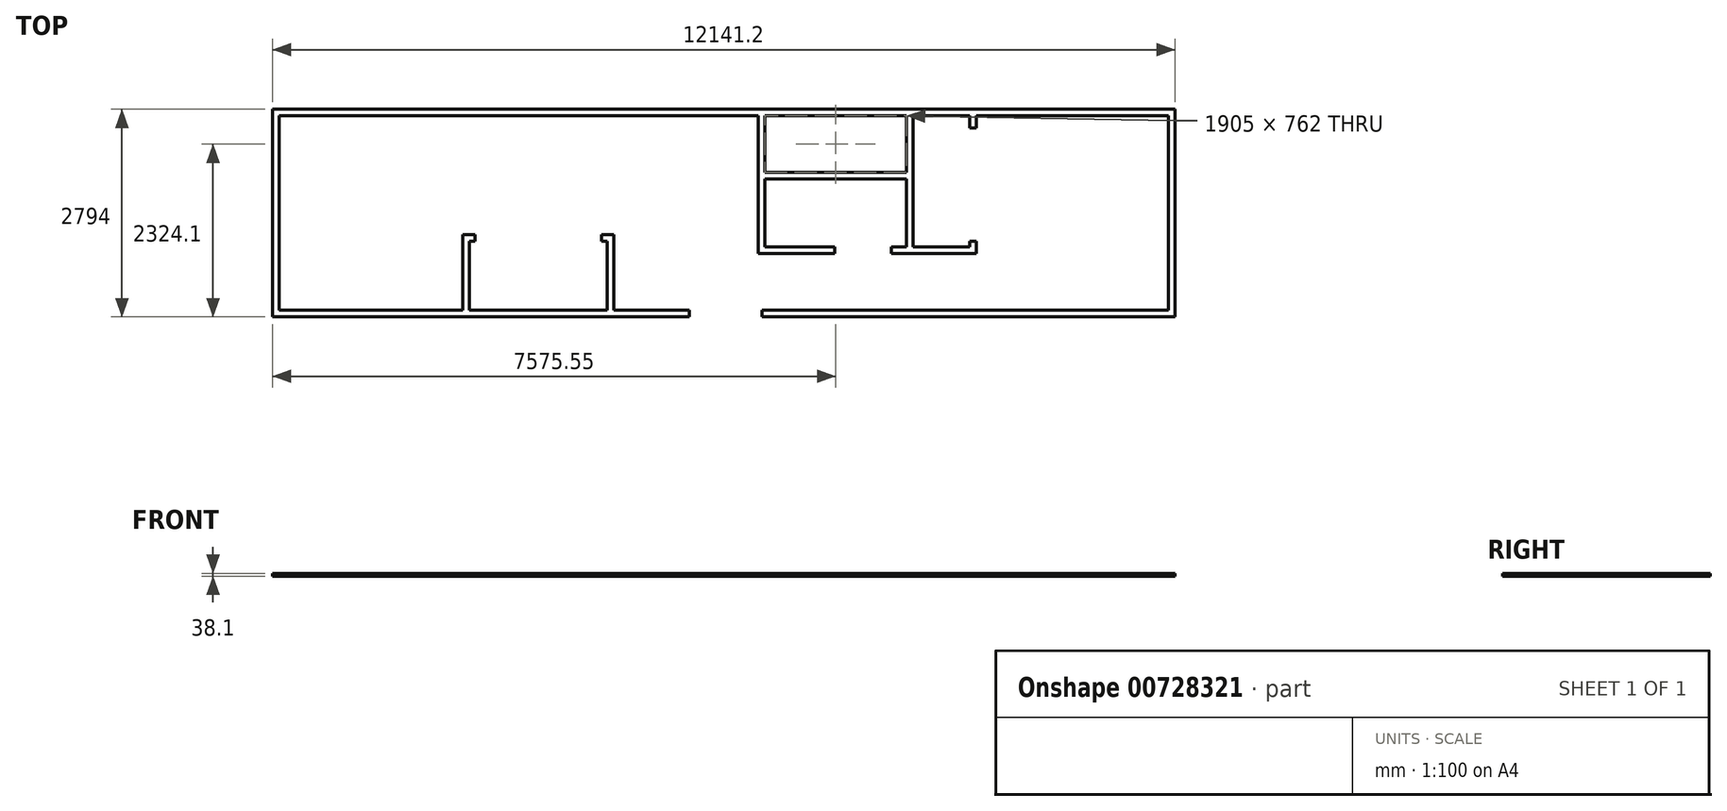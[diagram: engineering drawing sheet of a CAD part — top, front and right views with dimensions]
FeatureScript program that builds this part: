
annotation { "Feature Type Name" : "Feature", "Feature Type Description" : "" }
export const myFeature = defineFeature(function(context is Context, id is Id, definition is map)
    precondition{}
    {
        {
            var Q0;
            Q0=qCreatedBy(makeId("Top.planeOp"),FACE);
            var sketch = newSketch(context, id + "F0", { "sketchPlane" : qUnion([Q0])});
            skLineSegment(sketch, "E0.bottom", {"start": v(-6070.6, -1397) * mm, "end": v(-463.55, -1397) * mm});
            skLineSegment(sketch, "E0.top", {"start": v(-6070.6, 1397) * mm, "end": v(6070.6, 1397) * mm});
            skLineSegment(sketch, "E0.left", {"start": v(-6070.6, -1397) * mm, "end": v(-6070.6, 1397) * mm});
            skLineSegment(sketch, "E0.right", {"start": v(6070.6, -1397) * mm, "end": v(6070.6, 1397) * mm});
            skPoint(sketch, "E0.middle", {"position": v(0, 0) * mm});
            skLineSegment(sketch, "E1.0", {"start": v(-5981.7, -1308.1) * mm, "end": v(-5981.7, 1308.1) * mm});
            skLineSegment(sketch, "E1.1", {"start": v(-5981.7, -1308.1) * mm, "end": v(-463.55, -1308.1) * mm});
            skLineSegment(sketch, "E1.2", {"start": v(5981.7, -1308.1) * mm, "end": v(5981.7, 1308.1) * mm});
            skLineSegment(sketch, "E1.3", {"start": v(-5981.7, 1308.1) * mm, "end": v(463.55, 1308.1) * mm});
            skLineSegment(sketch, "E2.top", {"start": v(3397.25, -546.1) * mm, "end": v(3308.35, -546.1) * mm});
            skLineSegment(sketch, "E2.left", {"start": v(3397.25, 1308.1) * mm, "end": v(3397.25, 1143) * mm});
            skLineSegment(sketch, "E2.right", {"start": v(3308.35, 1308.1) * mm, "end": v(3308.35, 1143) * mm});
            skLineSegment(sketch, "E3.top", {"start": v(2457.45, -546.1) * mm, "end": v(2546.35, -546.1) * mm});
            skLineSegment(sketch, "E3.left", {"start": v(2457.45, 1308.1) * mm, "end": v(2457.45, 546.1) * mm});
            skLineSegment(sketch, "E3.right", {"start": v(2546.35, 1308.1) * mm, "end": v(2546.35, -457.2) * mm});
            skLineSegment(sketch, "E4", {"start": v(2546.35, -546.1) * mm, "end": v(3308.35, -546.1) * mm});
            skLineSegment(sketch, "E5.0", {"start": v(2546.35, -457.2) * mm, "end": v(3308.35, -457.2) * mm});
            skLineSegment(sketch, "E6.trimOffspring", {"start": v(2546.35, 1308.1) * mm, "end": v(3308.35, 1308.1) * mm});
            skLineSegment(sketch, "E7.trimOffspring", {"start": v(3397.25, 1308.1) * mm, "end": v(5981.7, 1308.1) * mm});
            skLineSegment(sketch, "E8", {"start": v(3308.35, 1143) * mm, "end": v(3397.25, 1143) * mm});
            skLineSegment(sketch, "E9", {"start": v(3308.35, -381) * mm, "end": v(3397.25, -381) * mm});
            skLineSegment(sketch, "E10", {"start": v(2457.45, -546.1) * mm, "end": v(2254.25, -546.1) * mm});
            skLineSegment(sketch, "E11", {"start": v(2457.45, -457.2) * mm, "end": v(2254.25, -457.2) * mm});
            skLineSegment(sketch, "E12", {"start": v(2254.25, -457.2) * mm, "end": v(2254.25, -546.1) * mm});
            skLineSegment(sketch, "E13.bottom", {"start": v(552.45, 546.1) * mm, "end": v(2457.45, 546.1) * mm});
            skLineSegment(sketch, "E14.trimOffspring", {"start": v(3308.35, -381) * mm, "end": v(3308.35, -457.2) * mm});
            skLineSegment(sketch, "E15.trimOffspring", {"start": v(3397.25, -381) * mm, "end": v(3397.25, -546.1) * mm});
            skLineSegment(sketch, "E16.trimOffspring", {"start": v(514.35, -1308.1) * mm, "end": v(5981.7, -1308.1) * mm});
            skLineSegment(sketch, "E17", {"start": v(-463.55, -1308.1) * mm, "end": v(-463.55, -1397) * mm});
            skLineSegment(sketch, "E18.trimOffspring", {"start": v(2457.45, 461.18) * mm, "end": v(2457.45, -457.2) * mm});
            skLineSegment(sketch, "E19.trimOffspring", {"start": v(552.45, 1308.1) * mm, "end": v(2457.45, 1308.1) * mm});
            skLineSegment(sketch, "E20", {"start": v(514.35, -1308.1) * mm, "end": v(514.35, -1397) * mm});
            skLineSegment(sketch, "E21.bottom", {"start": v(-1479.55, -1308.1) * mm, "end": v(-1568.45, -1308.1) * mm});
            skLineSegment(sketch, "E21.top", {"start": v(-1479.55, -292.1) * mm, "end": v(-1568.45, -292.1) * mm});
            skLineSegment(sketch, "E21.left", {"start": v(-1479.55, -1308.1) * mm, "end": v(-1479.55, -292.1) * mm});
            skLineSegment(sketch, "E21.right", {"start": v(-1568.45, -1308.1) * mm, "end": v(-1568.45, -292.1) * mm});
            skLineSegment(sketch, "E22.bottom", {"start": v(-3511.55, -292.1) * mm, "end": v(-3422.65, -292.1) * mm});
            skLineSegment(sketch, "E22.top", {"start": v(-3511.55, -1308.1) * mm, "end": v(-3422.65, -1308.1) * mm});
            skLineSegment(sketch, "E22.left", {"start": v(-3511.55, -292.1) * mm, "end": v(-3511.55, -1308.1) * mm});
            skLineSegment(sketch, "E22.right", {"start": v(-3422.65, -292.1) * mm, "end": v(-3422.65, -1308.1) * mm});
            skLineSegment(sketch, "E23", {"start": v(-3422.65, -292.1) * mm, "end": v(-3346.45, -292.1) * mm});
            skLineSegment(sketch, "E24", {"start": v(-3346.45, -292.1) * mm, "end": v(-3346.45, -381) * mm});
            skLineSegment(sketch, "E25", {"start": v(-3346.45, -381) * mm, "end": v(-3422.65, -381) * mm});
            skLineSegment(sketch, "E26.bottom", {"start": v(-1568.45, -292.1) * mm, "end": v(-1644.65, -292.1) * mm});
            skLineSegment(sketch, "E26.top", {"start": v(-1568.45, -381) * mm, "end": v(-1644.65, -381) * mm});
            skLineSegment(sketch, "E26.left", {"start": v(-1568.45, -292.1) * mm, "end": v(-1568.45, -381) * mm});
            skLineSegment(sketch, "E26.right", {"start": v(-1644.65, -292.1) * mm, "end": v(-1644.65, -381) * mm});
            skLineSegment(sketch, "E27", {"start": v(-3422.65, 1308.1) * mm, "end": v(-3422.65, 1397) * mm});
            skLineSegment(sketch, "E28", {"start": v(-4997.45, 1308.1) * mm, "end": v(-4997.45, 1397) * mm});
            skLineSegment(sketch, "E29.trimOffspring", {"start": v(514.35, -1397) * mm, "end": v(6070.6, -1397) * mm});
            skLineSegment(sketch, "E30", {"start": v(1492.25, -545.75) * mm, "end": v(1492.25, -456.85) * mm});
            skLineSegment(sketch, "E31", {"start": v(463.55, 1308.1) * mm, "end": v(463.55, -545.75) * mm});
            skLineSegment(sketch, "E32", {"start": v(463.55, -545.75) * mm, "end": v(1492.25, -545.75) * mm});
            skLineSegment(sketch, "E33", {"start": v(1492.25, -456.85) * mm, "end": v(552.45, -456.85) * mm});
            skLineSegment(sketch, "E34", {"start": v(552.45, -456.85) * mm, "end": v(552.45, 1308.1) * mm});
            skLineSegment(sketch, "E35", {"start": v(2457.45, 461.18) * mm, "end": v(552.45, 461.18) * mm});
            skSolve(sketch);
        }
        {
            var Q0;
            Q0=qSketchRegion(id+"F0",true);
            extrude(context, id + "F1", {"entities" : qUnion([Q0]), "depth" : 38.1 * mm, "offsetDistance" : 25.4 * mm});
        }
    });
